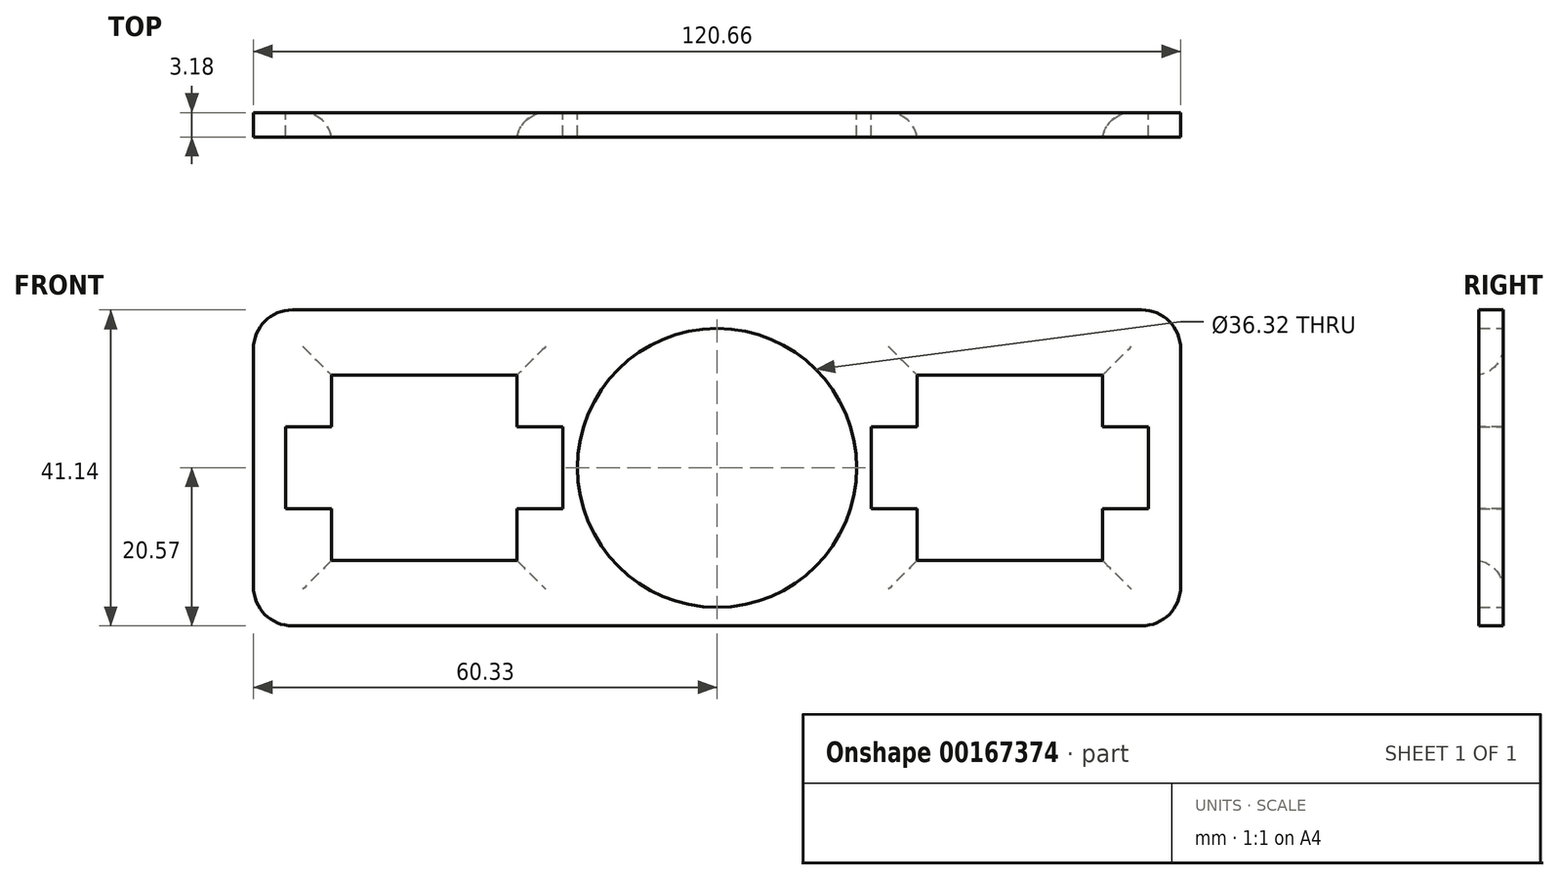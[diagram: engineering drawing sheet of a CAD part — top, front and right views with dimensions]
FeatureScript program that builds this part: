
annotation { "Feature Type Name" : "Feature", "Feature Type Description" : "" }
export const myFeature = defineFeature(function(context is Context, id is Id, definition is map)
    precondition{}
    {
        {
            var Q0;
            Q0=qCreatedBy(makeId("Front.planeOp"),FACE);
            var sketch = newSketch(context, id + "F0", { "sketchPlane" : qUnion([Q0])});
            skCircle(sketch, "E0", {"center": v(0, 0) * mm, "radius": 18.16 * mm});
            skLineSegment(sketch, "E1.bottom", {"start": v(-20.07, 5.33) * mm, "end": v(-56.13, 5.33) * mm});
            skLineSegment(sketch, "E1.top", {"start": v(-20.07, -5.33) * mm, "end": v(-56.13, -5.33) * mm});
            skLineSegment(sketch, "E1.left", {"start": v(-20.07, 5.33) * mm, "end": v(-20.07, -5.33) * mm});
            skLineSegment(sketch, "E1.right", {"start": v(-56.13, 5.33) * mm, "end": v(-56.13, -5.33) * mm});
            skLineSegment(sketch, "E2.bottom", {"start": v(56.13, 5.33) * mm, "end": v(20.07, 5.33) * mm});
            skLineSegment(sketch, "E2.top", {"start": v(56.13, -5.33) * mm, "end": v(20.07, -5.33) * mm});
            skLineSegment(sketch, "E2.left", {"start": v(56.13, 5.33) * mm, "end": v(56.13, -5.33) * mm});
            skLineSegment(sketch, "E2.right", {"start": v(20.07, 5.33) * mm, "end": v(20.07, -5.33) * mm});
            skPoint(sketch, "E2.middle", {"position": v(38.1, 0) * mm});
            skLineSegment(sketch, "E3.bottom", {"start": v(50.16, 12.07) * mm, "end": v(26.04, 12.07) * mm});
            skLineSegment(sketch, "E3.top", {"start": v(50.17, -12.06) * mm, "end": v(26.04, -12.07) * mm});
            skLineSegment(sketch, "E3.left", {"start": v(50.16, 12.07) * mm, "end": v(50.17, -12.06) * mm});
            skLineSegment(sketch, "E3.right", {"start": v(26.04, 12.07) * mm, "end": v(26.04, -12.07) * mm});
            skLineSegment(sketch, "E4.bottom", {"start": v(-26.04, 12.07) * mm, "end": v(-50.16, 12.06) * mm});
            skLineSegment(sketch, "E4.top", {"start": v(-26.03, -12.06) * mm, "end": v(-50.16, -12.07) * mm});
            skLineSegment(sketch, "E4.left", {"start": v(-26.03, 12.07) * mm, "end": v(-26.03, -12.06) * mm});
            skLineSegment(sketch, "E4.right", {"start": v(-50.16, 12.06) * mm, "end": v(-50.16, -12.07) * mm});
            skPoint(sketch, "E5.visualSharp", {"position": v(-60.32, 20.57) * mm});
            skLineSegment(sketch, "E6.bottom", {"start": v(60.33, 20.57) * mm, "end": v(-60.33, 20.57) * mm});
            skLineSegment(sketch, "E6.left", {"start": v(60.33, 20.57) * mm, "end": v(60.33, -20.57) * mm});
            skLineSegment(sketch, "E6.right", {"start": v(-60.33, 20.57) * mm, "end": v(-60.33, -20.57) * mm});
            skLineSegment(sketch, "E7.top", {"start": v(-60.33, -20.57) * mm, "end": v(60.33, -20.57) * mm});
            skLineSegment(sketch, "E8", {"start": v(-20.07, 0) * mm, "end": v(20.07, 0) * mm, "construction": true});
            skPoint(sketch, "E9", {"position": v(60.33, 0) * mm});
            skLineSegment(sketch, "E10", {"start": v(0, 20.57) * mm, "end": v(0, -20.57) * mm, "construction": true});
            skPoint(sketch, "E11", {"position": v(38.1, 5.33) * mm});
            skPoint(sketch, "E12", {"position": v(-38.1, 12.07) * mm});
            skPoint(sketch, "E13", {"position": v(-38.1, 0) * mm});
            skPoint(sketch, "E13.positionSnap0", {"position": v(-38.1, -5.33) * mm});
            skSolve(sketch);
        }
        {
            var Q0;
            Q0=makeQuery(id+"F0.imprint","IMPRINT",FACE,{"disambiguationData":[TD([[makeQuery(id+"F0.imprint","IMPRINT",EDGE,{"derivedFrom":sQuery(id+"F0.wireOp",EDGE,"E0")}),-1.0]])]});
            var Q1;
            Q1=makeQuery(id+"F0.imprint","IMPRINT",FACE,{"disambiguationData":[TD([[makeQuery(id+"F0.imprint","IMPRINT",EDGE,{"derivedFrom":sQuery(id+"F0.wireOp",EDGE,"E7.bottom")}),1.0]])]});
            extrude(context, id + "F1", {"entities" : qUnion([Q0, Q1]), "depth" : 3.17 * mm});
        }
        {
            var Q0;
            Q0=makeQuery(id+"F1.opExtrude","CAP_EDGE",EDGE,{"disambiguationData":[OSD([sQuery(id+"F0.wireOp",EDGE,"E3.bottom")])],"isStart":true});
            var Q1;
            {var subQ0=sQuery(id+"F0.wireOp",EDGE,"E3.right");Q1=makeQuery(id+"F1.opExtrude","CAP_EDGE",EDGE,{"disambiguationData":[OSD([subQ0]),TDD([makeQuery(id+"F0.imprint","IMPRINT",EDGE,{"disambiguationData":[TD([[makeQuery(id+"F0.imprint","INTERSECT",VERTEX,{"derivedFrom":[sQuery(id+"F0.wireOp",EDGE,"E3.bottom"),subQ0]}),-1.0]])],"derivedFrom":subQ0})])],"isStart":true});}
            var Q2;
            {var subQ0=sQuery(id+"F0.wireOp",EDGE,"E3.left");Q2=makeQuery(id+"F1.opExtrude","CAP_EDGE",EDGE,{"disambiguationData":[OSD([subQ0]),TDD([makeQuery(id+"F0.imprint","IMPRINT",EDGE,{"disambiguationData":[TD([[makeQuery(id+"F0.imprint","INTERSECT",VERTEX,{"derivedFrom":[sQuery(id+"F0.wireOp",EDGE,"E3.bottom"),subQ0]}),-1.0]])],"derivedFrom":subQ0})])],"isStart":true});}
            var Q3;
            {var subQ0=sQuery(id+"F0.wireOp",EDGE,"E4.left");Q3=makeQuery(id+"F1.opExtrude","CAP_EDGE",EDGE,{"disambiguationData":[OSD([subQ0]),TDD([makeQuery(id+"F0.imprint","IMPRINT",EDGE,{"disambiguationData":[TD([[makeQuery(id+"F0.imprint","INTERSECT",VERTEX,{"derivedFrom":[sQuery(id+"F0.wireOp",EDGE,"E4.bottom"),subQ0]}),-1.0]])],"derivedFrom":subQ0})])],"isStart":true});}
            var Q4;
            Q4=makeQuery(id+"F1.opExtrude","CAP_EDGE",EDGE,{"disambiguationData":[OSD([sQuery(id+"F0.wireOp",EDGE,"E4.bottom")])],"isStart":true});
            var Q5;
            {var subQ0=sQuery(id+"F0.wireOp",EDGE,"E4.right");Q5=makeQuery(id+"F1.opExtrude","CAP_EDGE",EDGE,{"disambiguationData":[OSD([subQ0]),TDD([makeQuery(id+"F0.imprint","IMPRINT",EDGE,{"disambiguationData":[TD([[makeQuery(id+"F0.imprint","INTERSECT",VERTEX,{"derivedFrom":[sQuery(id+"F0.wireOp",EDGE,"E4.bottom"),subQ0]}),-1.0]])],"derivedFrom":subQ0})])],"isStart":true});}
            var Q6;
            {var subQ0=sQuery(id+"F0.wireOp",EDGE,"E4.right");Q6=makeQuery(id+"F1.opExtrude","CAP_EDGE",EDGE,{"disambiguationData":[OSD([subQ0]),TDD([makeQuery(id+"F0.imprint","IMPRINT",EDGE,{"disambiguationData":[TD([[makeQuery(id+"F0.imprint","INTERSECT",VERTEX,{"derivedFrom":[sQuery(id+"F0.wireOp",EDGE,"E4.top"),subQ0]}),1.0]])],"derivedFrom":subQ0})])],"isStart":true});}
            var Q7;
            Q7=makeQuery(id+"F1.opExtrude","CAP_EDGE",EDGE,{"disambiguationData":[OSD([sQuery(id+"F0.wireOp",EDGE,"E4.top")])],"isStart":true});
            var Q8;
            {var subQ0=sQuery(id+"F0.wireOp",EDGE,"E4.left");Q8=makeQuery(id+"F1.opExtrude","CAP_EDGE",EDGE,{"disambiguationData":[OSD([subQ0]),TDD([makeQuery(id+"F0.imprint","IMPRINT",EDGE,{"disambiguationData":[TD([[makeQuery(id+"F0.imprint","INTERSECT",VERTEX,{"derivedFrom":[sQuery(id+"F0.wireOp",EDGE,"E4.top"),subQ0]}),1.0]])],"derivedFrom":subQ0})])],"isStart":true});}
            var Q9;
            {var subQ0=sQuery(id+"F0.wireOp",EDGE,"E3.right");Q9=makeQuery(id+"F1.opExtrude","CAP_EDGE",EDGE,{"disambiguationData":[OSD([subQ0]),TDD([makeQuery(id+"F0.imprint","IMPRINT",EDGE,{"disambiguationData":[TD([[makeQuery(id+"F0.imprint","INTERSECT",VERTEX,{"derivedFrom":[sQuery(id+"F0.wireOp",EDGE,"E3.top"),subQ0]}),1.0]])],"derivedFrom":subQ0})])],"isStart":true});}
            var Q10;
            Q10=makeQuery(id+"F1.opExtrude","CAP_EDGE",EDGE,{"disambiguationData":[OSD([sQuery(id+"F0.wireOp",EDGE,"E3.top")])],"isStart":true});
            var Q11;
            {var subQ0=sQuery(id+"F0.wireOp",EDGE,"E3.left");Q11=makeQuery(id+"F1.opExtrude","CAP_EDGE",EDGE,{"disambiguationData":[OSD([subQ0]),TDD([makeQuery(id+"F0.imprint","IMPRINT",EDGE,{"disambiguationData":[TD([[makeQuery(id+"F0.imprint","INTERSECT",VERTEX,{"derivedFrom":[sQuery(id+"F0.wireOp",EDGE,"E3.top"),subQ0]}),1.0]])],"derivedFrom":subQ0})])],"isStart":true});}
            fillet(context, id + "F2", {"entities" : qUnion([Q0, Q1, Q2, Q3, Q4, Q5, Q6, Q7, Q8, Q9, Q10, Q11]), "radius" : 3.8 * mm, "tangentPropagation" : true, "allowEdgeOverflow" : false});
        }
        {
            var Q0;
            Q0=makeQuery(id+"F1.opExtrude","SWEPT_EDGE",EDGE,{"disambiguationData":[OSD([sQuery(id+"F0.wireOp",EDGE,"E6.bottom"),sQuery(id+"F0.wireOp",EDGE,"E6.left")])]});
            var Q1;
            Q1=makeQuery(id+"F1.opExtrude","SWEPT_EDGE",EDGE,{"disambiguationData":[OSD([sQuery(id+"F0.wireOp",EDGE,"E6.bottom"),sQuery(id+"F0.wireOp",EDGE,"E6.right")])]});
            var Q2;
            Q2=makeQuery(id+"F1.opExtrude","SWEPT_EDGE",EDGE,{"disambiguationData":[OSD([sQuery(id+"F0.wireOp",EDGE,"E6.right"),sQuery(id+"F0.wireOp",EDGE,"E7.top")])]});
            var Q3;
            Q3=makeQuery(id+"F1.opExtrude","SWEPT_EDGE",EDGE,{"disambiguationData":[OSD([sQuery(id+"F0.wireOp",EDGE,"E6.left"),sQuery(id+"F0.wireOp",EDGE,"E7.top")])]});
            fillet(context, id + "F3", {"entities" : qUnion([Q0, Q1, Q2, Q3]), "radius" : 5.08 * mm, "tangentPropagation" : true, "allowEdgeOverflow" : false});
        }
    });
